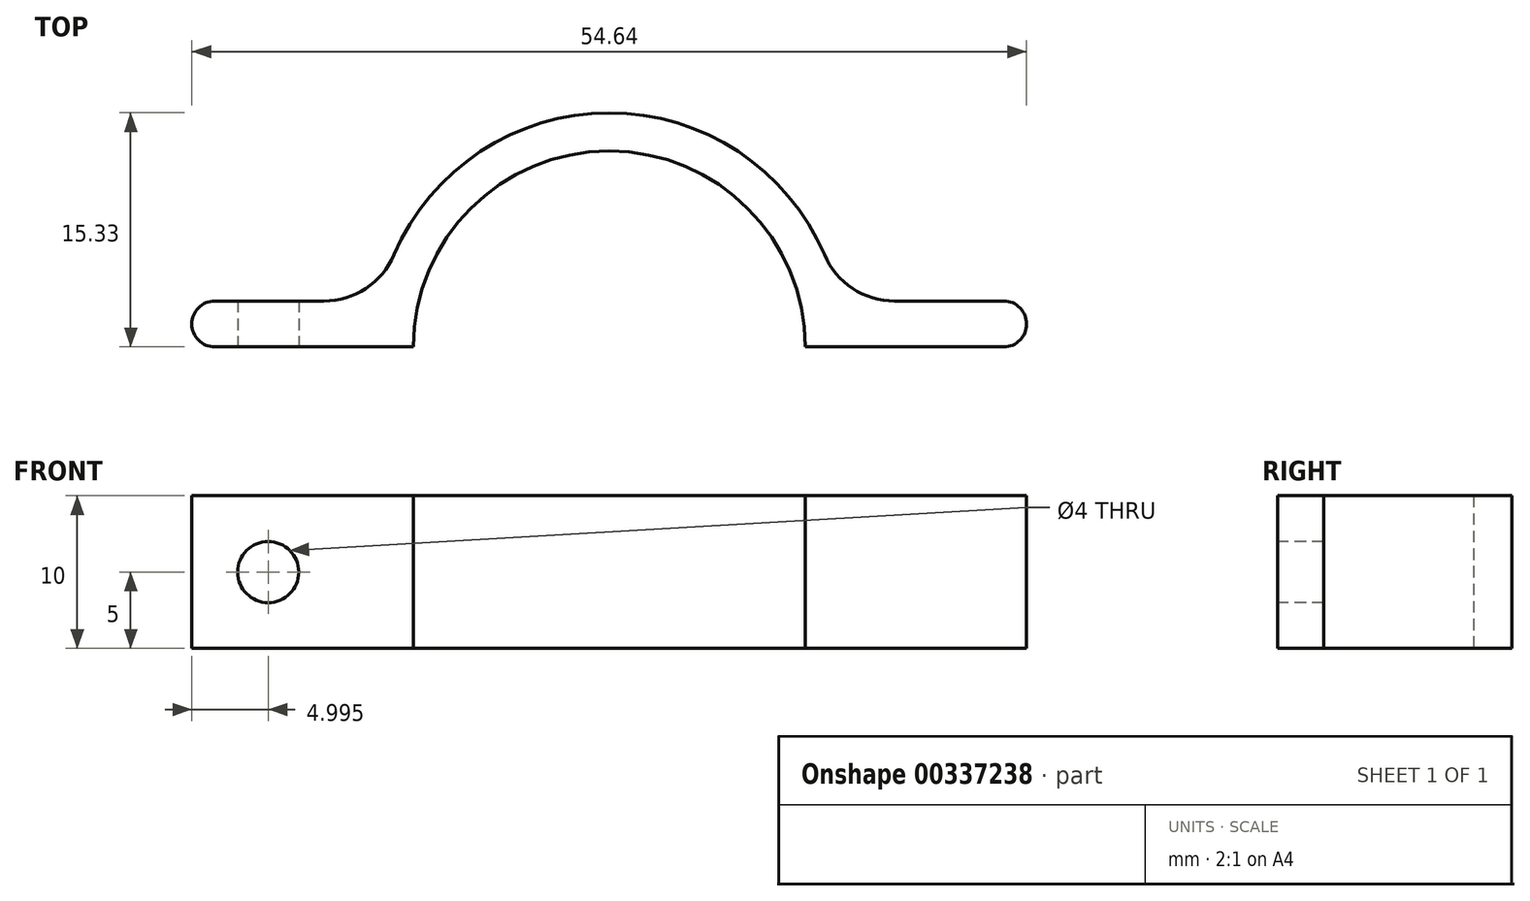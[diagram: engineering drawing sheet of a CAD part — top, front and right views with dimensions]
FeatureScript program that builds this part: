
annotation { "Feature Type Name" : "Feature", "Feature Type Description" : "" }
export const myFeature = defineFeature(function(context is Context, id is Id, definition is map)
    precondition{}
    {
        {
            var Q0;
            Q0=qCreatedBy(makeId("Top.planeOp"),FACE);
            var sketch = newSketch(context, id + "F0", { "sketchPlane" : qUnion([Q0])});
            skCircle(sketch, "E0", {"center": v(0, 0) * mm, "radius": 12.82 * mm, "construction": true});
            skCircle(sketch, "E1", {"center": v(0, 0) * mm, "radius": 15.32 * mm, "construction": true});
            skLineSegment(sketch, "E2.bottom", {"start": v(27.33, -3) * mm, "end": v(-27.33, -3) * mm, "construction": true});
            skLineSegment(sketch, "E2.top", {"start": v(27.33, 3) * mm, "end": v(-27.33, 3) * mm, "construction": true});
            skLineSegment(sketch, "E2.left", {"start": v(27.33, -3) * mm, "end": v(27.33, 3) * mm, "construction": true});
            skLineSegment(sketch, "E2.right", {"start": v(-27.33, -3) * mm, "end": v(-27.33, 3) * mm, "construction": true});
            skLineSegment(sketch, "E3", {"start": v(-27.33, 3) * mm, "end": v(-27.33, 0) * mm});
            skLineSegment(sketch, "E4", {"start": v(-27.33, 0) * mm, "end": v(27.33, 0) * mm, "construction": true});
            skLineSegment(sketch, "E5", {"start": v(27.33, 0) * mm, "end": v(27.33, 3) * mm});
            skLineSegment(sketch, "E6", {"start": v(15.03, 3) * mm, "end": v(27.33, 3) * mm});
            skLineSegment(sketch, "E7", {"start": v(-15.03, 3) * mm, "end": v(-27.33, 3) * mm});
            skLineSegment(sketch, "E8", {"start": v(0, 0) * mm, "end": v(0, 20.73) * mm, "construction": true});
            skArc(sketch, "E9", {"start": v(15.03, 3) * mm, "mid": v(0, 15.32) * mm, "end": v(-15.03, 3) * mm});
            skLineSegment(sketch, "E10", {"start": v(-12.82, 0) * mm, "end": v(-27.33, 0) * mm});
            skLineSegment(sketch, "E11", {"start": v(27.33, 0) * mm, "end": v(12.82, 0) * mm});
            skLineSegment(sketch, "E12", {"start": v(12.82, 0) * mm, "end": v(27.33, 0) * mm});
            skArc(sketch, "E13", {"start": v(12.82, 0) * mm, "mid": v(0, 12.82) * mm, "end": v(-12.82, 0) * mm});
            skSolve(sketch);
        }
        {
            var Q0;
            Q0=makeQuery(id+"F0.imprint","IMPRINT",FACE,{"disambiguationData":[TD([[makeQuery(id+"F0.imprint","IMPRINT",EDGE,{"derivedFrom":sQuery(id+"F0.wireOp",EDGE,"E3")}),1.0]])]});
            extrude(context, id + "F1", {"entities" : qUnion([Q0]), "depth" : 10 * mm});
        }
        {
            var Q0;
            Q0=makeQuery(id+"F1.opExtrude","SWEPT_FACE",FACE,{"disambiguationData":[OSD([sQuery(id+"F0.wireOp",EDGE,"E10")])]});
            var sketch = newSketch(context, id + "F2", { "sketchPlane" : qUnion([Q0])});
            skLineSegment(sketch, "E14", {"start": v(0, 0) * mm, "end": v(0, 21.08) * mm, "construction": true});
            skLineSegment(sketch, "E15", {"start": v(-27.33, 5) * mm, "end": v(31.85, 5) * mm, "construction": true});
            skLineSegment(sketch, "E16", {"start": v(-20.08, 10) * mm, "end": v(-20.08, -4.36) * mm, "construction": true});
            skCircle(sketch, "E17", {"center": v(-22.33, 5) * mm, "radius": 2 * mm});
            skCircle(sketch, "E18.MirrorC", {"center": v(22.33, 5) * mm, "radius": 2 * mm});
            skSolve(sketch);
        }
        {
            var Q0;
            Q0=makeQuery(id+"F2.imprint","IMPRINT",FACE,{"disambiguationData":[TD([[makeQuery(id+"F2.imprint","IMPRINT",EDGE,{"derivedFrom":sQuery(id+"F2.wireOp",EDGE,"E17")}),1.0]])]});
            var Q1;
            Q1=makeQuery(id+"F2.imprint","IMPRINT",FACE,{"disambiguationData":[TD([[makeQuery(id+"F2.imprint","IMPRINT",EDGE,{"derivedFrom":sQuery(id+"F2.wireOp",EDGE,"E18.MirrorC")}),-1.0]])]});
            var Q2;
            Q2=sQuery(id+"F2.wireOp",EDGE,"E17");
            var Q3;
            Q3=sQuery(id+"F2.wireOp",EDGE,"E18.MirrorC");
            extrude(context, id + "F3", {"entities" : qUnion([Q0, Q1]), "operationType" : NewBodyOperationType.REMOVE, "surfaceEntities" : qUnion([Q2, Q3]), "endBound" : BoundingType.THROUGH_ALL, "oppositeDirection" : true, "depth" : 25 * mm});
        }
        {
            var Q0;
            Q0=makeQuery(id+"F1.opExtrude","SWEPT_EDGE",EDGE,{"disambiguationData":[OSD([sQuery(id+"F0.wireOp",EDGE,"E7"),sQuery(id+"F0.wireOp",EDGE,"E9")])]});
            var Q1;
            Q1=makeQuery(id+"F1.opExtrude","SWEPT_EDGE",EDGE,{"disambiguationData":[OSD([sQuery(id+"F0.wireOp",EDGE,"E6"),sQuery(id+"F0.wireOp",EDGE,"E9")])]});
            fillet(context, id + "F4", {"entities" : qUnion([Q0, Q1]), "radius" : 5 * mm, "tangentPropagation" : true, "allowEdgeOverflow" : false});
        }
        {
            var Q0;
            Q0=makeQuery(id+"F1.opExtrude","SWEPT_EDGE",EDGE,{"disambiguationData":[OSD([sQuery(id+"F0.wireOp",EDGE,"E3"),sQuery(id+"F0.wireOp",EDGE,"E10")])]});
            var Q1;
            Q1=makeQuery(id+"F1.opExtrude","SWEPT_EDGE",EDGE,{"disambiguationData":[OSD([sQuery(id+"F0.wireOp",EDGE,"E3"),sQuery(id+"F0.wireOp",EDGE,"E7")])]});
            var Q2;
            Q2=makeQuery(id+"F1.opExtrude","SWEPT_EDGE",EDGE,{"disambiguationData":[OSD([sQuery(id+"F0.wireOp",EDGE,"E5"),sQuery(id+"F0.wireOp",EDGE,"E12")])]});
            var Q3;
            Q3=makeQuery(id+"F1.opExtrude","SWEPT_EDGE",EDGE,{"disambiguationData":[OSD([sQuery(id+"F0.wireOp",EDGE,"E5"),sQuery(id+"F0.wireOp",EDGE,"E6")])]});
            fillet(context, id + "F5", {"entities" : qUnion([Q0, Q1, Q2, Q3]), "radius" : 1.5 * mm, "tangentPropagation" : true, "allowEdgeOverflow" : false});
        }
    });
